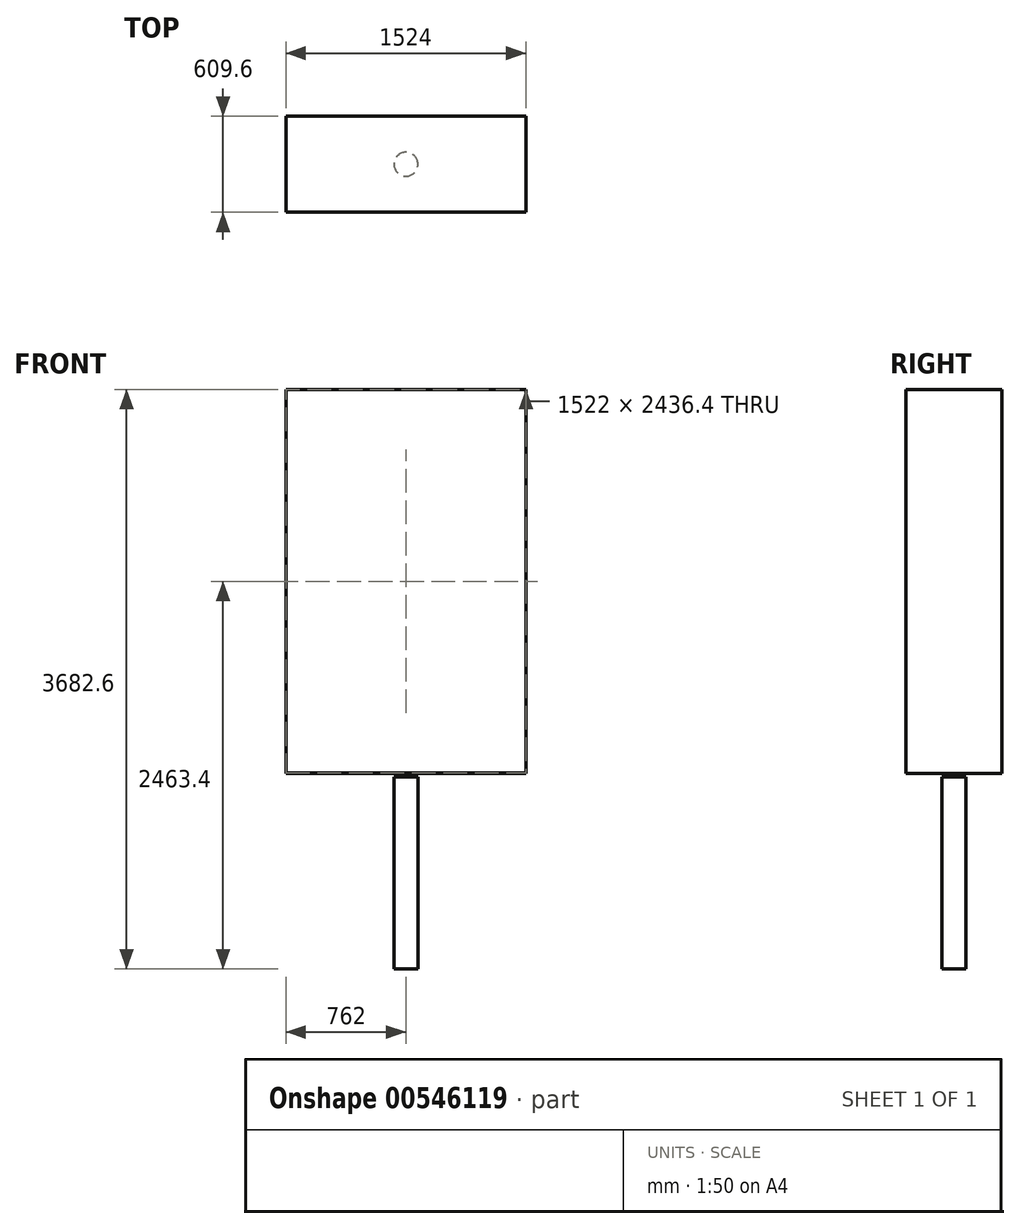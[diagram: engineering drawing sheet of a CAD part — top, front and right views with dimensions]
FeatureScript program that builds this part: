
annotation { "Feature Type Name" : "Feature", "Feature Type Description" : "" }
export const myFeature = defineFeature(function(context is Context, id is Id, definition is map)
    precondition{}
    {
        {
            var Q0;
            Q0=qCreatedBy(makeId("Top.planeOp"),FACE);
            var sketch = newSketch(context, id + "F0", { "sketchPlane" : qUnion([Q0])});
            skCircle(sketch, "E0", {"center": v(0, 0) * mm, "radius": 76.2 * mm});
            skSolve(sketch);
        }
        {
            var Q0;
            Q0 = qSketchRegion(id + "F0", true);
            extrude(context, id + "F1", {"entities" : qUnion([Q0]), "depth" : 1219.2 * mm, "offsetDistance" : 25 * mm});
        }
        {
            var Q0;
            Q0=makeQuery(id+"F1.opExtrude","CAP_FACE",FACE,{"disambiguationData":[OSD([sQuery(id+"F0.wireOp",EDGE,"E0")])],"isStart":false});
            cPlane(context, id + "F2", {"entities" : qUnion([Q0]), "cplaneType" : CPlaneType.OFFSET, "offset" : 25 * mm, "width" : 150 * mm, "height" : 150 * mm});
        }
        {
            var Q0;
            Q0=qCreatedBy(id+"F2.planeOp",FACE);
            var sketch = newSketch(context, id + "F3", { "sketchPlane" : qUnion([Q0])});
            skLineSegment(sketch, "E1.bottom", {"start": v(-762, 304.8) * mm, "end": v(762, 304.8) * mm});
            skLineSegment(sketch, "E1.top", {"start": v(-762, -304.8) * mm, "end": v(762, -304.8) * mm});
            skLineSegment(sketch, "E1.left", {"start": v(-762, 304.8) * mm, "end": v(-762, -304.8) * mm});
            skLineSegment(sketch, "E1.right", {"start": v(762, 304.8) * mm, "end": v(762, -304.8) * mm});
            skPoint(sketch, "E1.middle", {"position": v(0, 0) * mm});
            skSolve(sketch);
        }
        {
            var Q0;
            Q0=makeQuery(id+"F3.imprint","IMPRINT",FACE,{"disambiguationData":[TD([[makeQuery(id+"F3.imprint","IMPRINT",EDGE,{"derivedFrom":sQuery(id+"F3.wireOp",EDGE,"E1.bottom")}),-1.0]])]});
            extrude(context, id + "F4", {"entities" : qUnion([Q0]), "depth" : 2438.4 * mm, "offsetDistance" : 25 * mm});
        }
        {
            var Q0;
            Q0=makeQuery(id+"F4.opExtrude","SWEPT_FACE",FACE,{"disambiguationData":[OSD([sQuery(id+"F3.wireOp",EDGE,"E1.top")])]});
            var Q1;
            Q1=makeQuery(id+"F4.opExtrude","SWEPT_FACE",FACE,{"disambiguationData":[OSD([sQuery(id+"F3.wireOp",EDGE,"E1.bottom")])]});
            shell(context, id + "F5", {"entities" : qUnion([Q0, Q1]), "thickness" : 1 * mm});
        }
        {
            var Q0;
            {var subQ0=sQuery(id+"F3.wireOp",EDGE,"E1.right");var subQ1=sQuery(id+"F3.wireOp",EDGE,"E1.left");var subQ2=sQuery(id+"F3.wireOp",EDGE,"E1.top");var subQ3=sQuery(id+"F3.wireOp",EDGE,"E1.bottom");Q0=makeQuery(id+"F5.opShell","OFFSET_FACE",FACE,{"disambiguationData":[OSD([subQ3,subQ2,subQ1,subQ0]),TDD([makeQuery(id+"F4.opExtrude","CAP_FACE",FACE,{"disambiguationData":[OSD([subQ3,subQ2,subQ1,subQ0])],"isStart":true})])]});}
            var sketch = newSketch(context, id + "F6", { "sketchPlane" : qUnion([Q0])});
            skLineSegment(sketch, "E2.bottom", {"start": v(-12.7, 25.4) * mm, "end": v(12.7, 25.4) * mm});
            skLineSegment(sketch, "E2.top", {"start": v(-12.7, -25.4) * mm, "end": v(12.7, -25.4) * mm});
            skLineSegment(sketch, "E2.left", {"start": v(-12.7, 25.4) * mm, "end": v(-12.7, -25.4) * mm});
            skLineSegment(sketch, "E2.right", {"start": v(12.7, 25.4) * mm, "end": v(12.7, -25.4) * mm});
            skPoint(sketch, "E2.middle", {"position": v(0, 0) * mm});
            skSolve(sketch);
        }
        {
            var Q0;
            Q0 = qSketchRegion(id + "F6", true);
            var Q1;
            Q1=sQuery(id+"F6.wireOp",EDGE,"E2.right");
            var Q2;
            Q2=sQuery(id+"F6.wireOp",EDGE,"E2.left");
            var Q3;
            Q3=sQuery(id+"F6.wireOp",EDGE,"E2.bottom");
            var Q4;
            Q4=sQuery(id+"F6.wireOp",EDGE,"E2.top");
            var Q5;
            {var subQ0=sQuery(id+"F3.wireOp",EDGE,"E1.right");var subQ1=sQuery(id+"F3.wireOp",EDGE,"E1.left");var subQ2=sQuery(id+"F3.wireOp",EDGE,"E1.top");var subQ3=sQuery(id+"F3.wireOp",EDGE,"E1.bottom");Q5=makeQuery(id+"F5.opShell","OFFSET_FACE",FACE,{"disambiguationData":[OSD([subQ3,subQ2,subQ1,subQ0]),TDD([makeQuery(id+"F4.opExtrude","CAP_FACE",FACE,{"disambiguationData":[OSD([subQ3,subQ2,subQ1,subQ0])],"isStart":false})])]});}
            extrude(context, id + "F7", {"entities" : qUnion([Q0]), "bodyType" : ToolBodyType.SURFACE, "operationType" : NewBodyOperationType.ADD, "surfaceEntities" : qUnion([Q1, Q2, Q3, Q4]), "endBound" : BoundingType.UP_TO_SURFACE, "depth" : 25 * mm, "endBoundEntityFace" : qUnion([Q5]), "offsetDistance" : 25 * mm});
        }
    });
